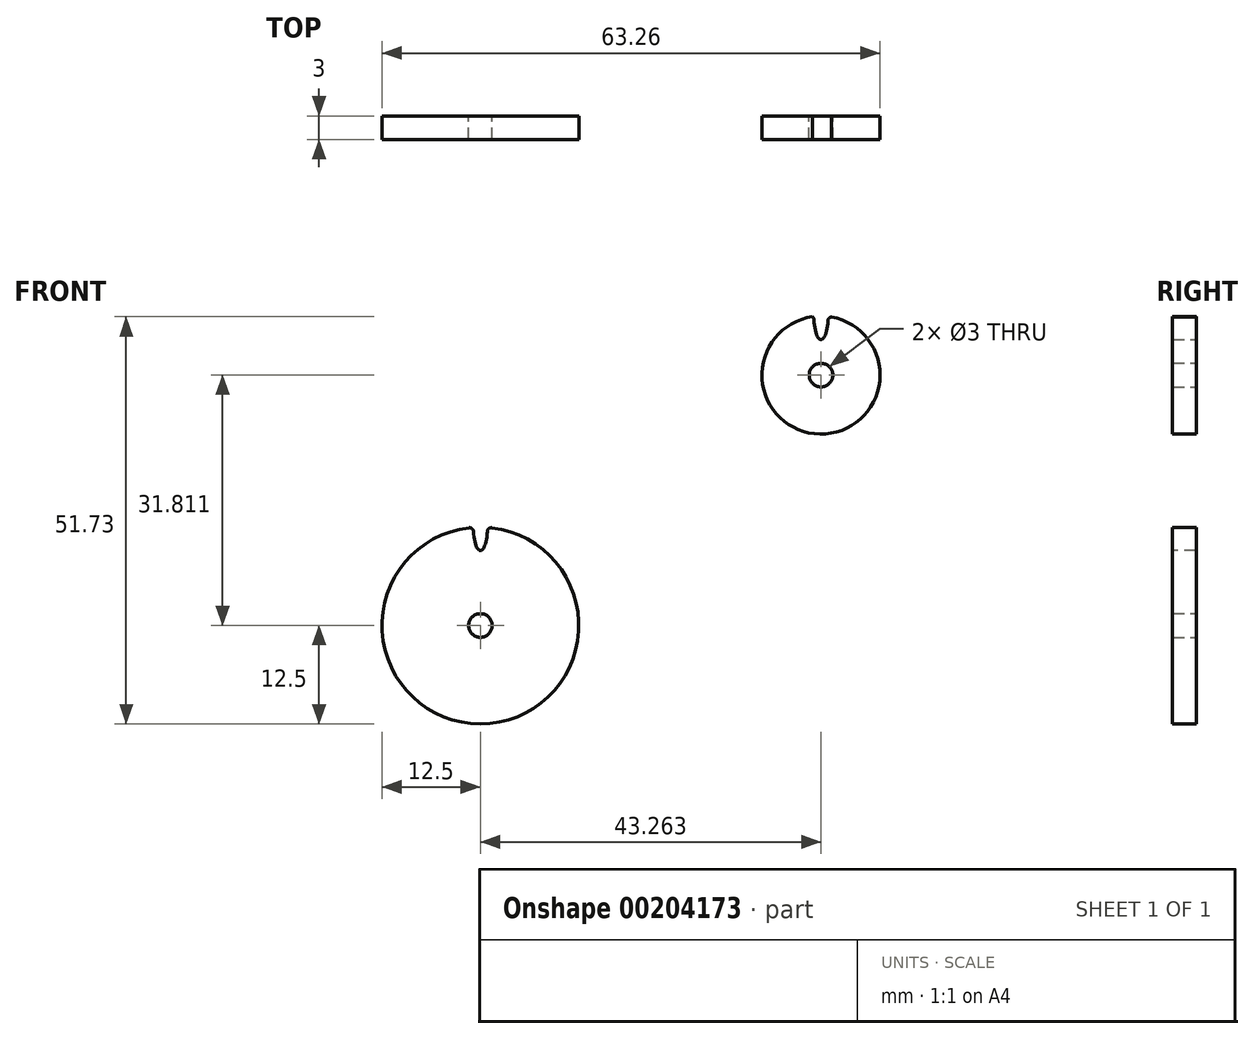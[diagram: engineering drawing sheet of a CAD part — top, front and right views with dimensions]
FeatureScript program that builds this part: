
annotation { "Feature Type Name" : "Feature", "Feature Type Description" : "" }
export const myFeature = defineFeature(function(context is Context, id is Id, definition is map)
    precondition{}
    {
        {
            var Q0;
            Q0=qCreatedBy(makeId("Front.planeOp"),FACE);
            var sketch = newSketch(context, id + "F0", { "sketchPlane" : qUnion([Q0])});
            skCircle(sketch, "E0", {"center": v(43.26, 31.81) * mm, "radius": 7.5 * mm});
            skCircle(sketch, "E1.converted", {"center": v(0, 0) * mm, "radius": 12.5 * mm});
            skCircle(sketch, "E2", {"center": v(0, 0) * mm, "radius": 1.5 * mm});
            skCircle(sketch, "E3", {"center": v(43.26, 31.81) * mm, "radius": 1.5 * mm});
            skSolve(sketch);
        }
        {
            var Q0;
            Q0 = qSketchRegion(id + "F0", true);
            extrude(context, id + "F1", {"entities" : qUnion([Q0]), "depth" : 3 * mm});
        }
        {
            var Q0;
            Q0=qCreatedBy(makeId("Front.planeOp"),FACE);
            var sketch = newSketch(context, id + "F2", { "sketchPlane" : qUnion([Q0])});
            skEllipticalArc(sketch, "E4", {});
            skLineSegment(sketch, "E5", {"start": v(0, 12.5) * mm, "end": v(0, 9.5) * mm});
            skPoint(sketch, "E6.visualSharp", {"position": v(-0.9, 12.47) * mm});
            skArc(sketch, "E6.filletArc", {"start": v(-0.88, 11.95) * mm, "mid": v(-1.06, 12.3) * mm, "end": v(-1.44, 12.42) * mm});
            skPoint(sketch, "E7.visualSharp", {"position": v(0.9, 12.47) * mm});
            skArc(sketch, "E7.filletArc", {"start": v(1.44, 12.42) * mm, "mid": v(1.06, 12.3) * mm, "end": v(0.88, 11.95) * mm});
            skLineSegment(sketch, "E8", {"start": v(0, 9.5) * mm, "end": v(0, 0) * mm});
            skArc(sketch, "E9", {"start": v(1.44, 12.42) * mm, "mid": v(0, 12.5) * mm, "end": v(-1.44, 12.42) * mm});
            const initialGuessF2  = {"E4": [0, 0.0125, 0, -1, 0.003, 0.0009000526291073121, 4.897452725529938, 1.38573258164965]};
            skSetInitialGuess(sketch, initialGuessF2);
            skSolve(sketch);
        }
        {
            var Q0;
            {var subQ0=sQuery(id+"F2.wireOp",EDGE,"E5");Q0=makeQuery(id+"F2.imprint","IMPRINT",FACE,{"disambiguationData":[TD([[makeQuery(id+"F2.imprint","IMPRINT",EDGE,{"derivedFrom":subQ0}),1.0]])]});}
            var Q1;
            {var subQ0=sQuery(id+"F2.wireOp",EDGE,"E5");Q1=makeQuery(id+"F2.imprint","IMPRINT",FACE,{"disambiguationData":[TD([[makeQuery(id+"F2.imprint","IMPRINT",EDGE,{"derivedFrom":subQ0}),-1.0]])]});}
            extrude(context, id + "F3", {"entities" : qUnion([Q0, Q1]), "operationType" : NewBodyOperationType.REMOVE, "endBound" : BoundingType.THROUGH_ALL, "depth" : 25 * mm});
        }
        {
            var Q0;
            Q0=makeQuery(id+"F1.opExtrude","CAP_FACE",FACE,{"disambiguationData":[OSD([sQuery(id+"F0.wireOp",EDGE,"E0")])],"isStart":true});
            var sketch = newSketch(context, id + "F4", { "sketchPlane" : qUnion([Q0])});
            skLineSegment(sketch, "E10", {"start": v(-43.26, 31.81) * mm, "end": v(-43.26, 39.31) * mm});
            skEllipticalArc(sketch, "E11", {});
            skArc(sketch, "E12", {"start": v(-42.18, 39.23) * mm, "mid": v(-43.4, 39.3) * mm, "end": v(-44.62, 39.19) * mm});
            skPoint(sketch, "E13.visualSharp", {"position": v(-42.36, 39.26) * mm});
            skArc(sketch, "E13.filletArc", {"start": v(-42.18, 39.23) * mm, "mid": v(-42.32, 39.07) * mm, "end": v(-42.37, 38.86) * mm});
            skPoint(sketch, "E14.visualSharp", {"position": v(-44.16, 39.26) * mm});
            skArc(sketch, "E14.filletArc", {"start": v(-44.15, 38.72) * mm, "mid": v(-44.3, 39.04) * mm, "end": v(-44.62, 39.19) * mm});
            skLineSegment(sketch, "E15", {"start": v(-43.26, 36.31) * mm, "end": v(-43.26, 39.31) * mm});
            const initialGuessF4  = {"E11": [-0.043263018131256104, 0.03931104362010956, 0, -1, 0.003, 0.0009001468952600006, 4.911027182480682, 1.4185474353675394]};
            skSetInitialGuess(sketch, initialGuessF4);
            skSolve(sketch);
        }
        {
            var Q0;
            Q0 = qSketchRegion(id + "F4", true);
            extrude(context, id + "F5", {"entities" : qUnion([Q0]), "operationType" : NewBodyOperationType.REMOVE, "endBound" : BoundingType.UP_TO_NEXT, "oppositeDirection" : true, "depth" : 25 * mm});
        }
    });
